SOLIDWORKS PART (.sldprt)
format: sldprt  version: not decoded by parser v0  size: 146,944 bytes
history: native  units: mm
features: sketch x3, extrude x2, material x1, fillet x1, cut_extrude x1 (+13 scaffold rows collapsed)
feature tree (21):
  scaffold x13  (default folders/planes/origin — collapsed)
  material  "Material <not specified>"
  sketch  "Sketch1"  dims[D1=18.0mm D2=25.0mm D3=~16.781521mm]
  extrude  "Boss-Extrude1"  Depth=3mm
  fillet  "Fillet1"  Radius=4mm
  sketch  "Sketch2"  dims[D2=8.0mm D1=1.0mm]
  extrude  "Boss-Extrude2"  Depth=1mm
  sketch  "Sketch5"  dims[D1=3.1mm]
  cut_extrude  "Cut-Extrude1"  [1 undecoded]
decode coverage: 6 of 7 modeling features carry decoded parameters
note: ~ marks probable driven/reference dimensions
note: 1 parameter value undecoded
note: suppression state not decoded; provenance and decode notes live in map.json
